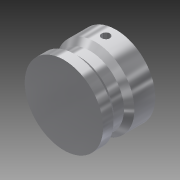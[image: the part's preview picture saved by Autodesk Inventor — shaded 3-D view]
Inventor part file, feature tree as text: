
AUTODESK INVENTOR PART (.ipt)
format: ipt  version: 2013 (Build 170138000, 138)  size: 120,832 bytes
history: native  units: in
note: dims shown in document units (in); Inventor stores cm internally (conversion verified against a paired STEP export)
features: sketch x3, hole x2, revolve x1, plane x1
ambient origin geometry x8: Origin, YZ Plane, XZ Plane, XY Plane, X Axis, Y Axis, Z Axis, Center Point
bodies: Solid1 (feature_tree)
feature tree (7):
  revolve  "Revolution1"  Angle=135.0deg
  hole  "Hole1"  [1 undecoded]
  plane  "Work Plane1"
  hole  "Hole2"  [1 undecoded]
  sketch  "Sketch1"  dims[d0=0.375in d1=135.0deg]
  sketch  "Sketch2"  dims[d2=0.1in d4=0.05in]
  sketch  "Sketch3"  dims[d5=0.5in d7=0.1in d8=90.0deg d9=0.1969in d10=0.75in d11=0.375in d12=0.25in d13=0.5635in d14=0.4375in d15=0.8108in d16=0.4in d17=0.0787in d18=0.75in d19=0.375in d20=0.25in d21=0.5635in d22=0.4375in d23=0.8108in]
note: 2 required parameter values undecoded (feature->parameter linkage not recoverable at this tier; creation-order binding heuristic only, values carry confidence <= 0.55)
